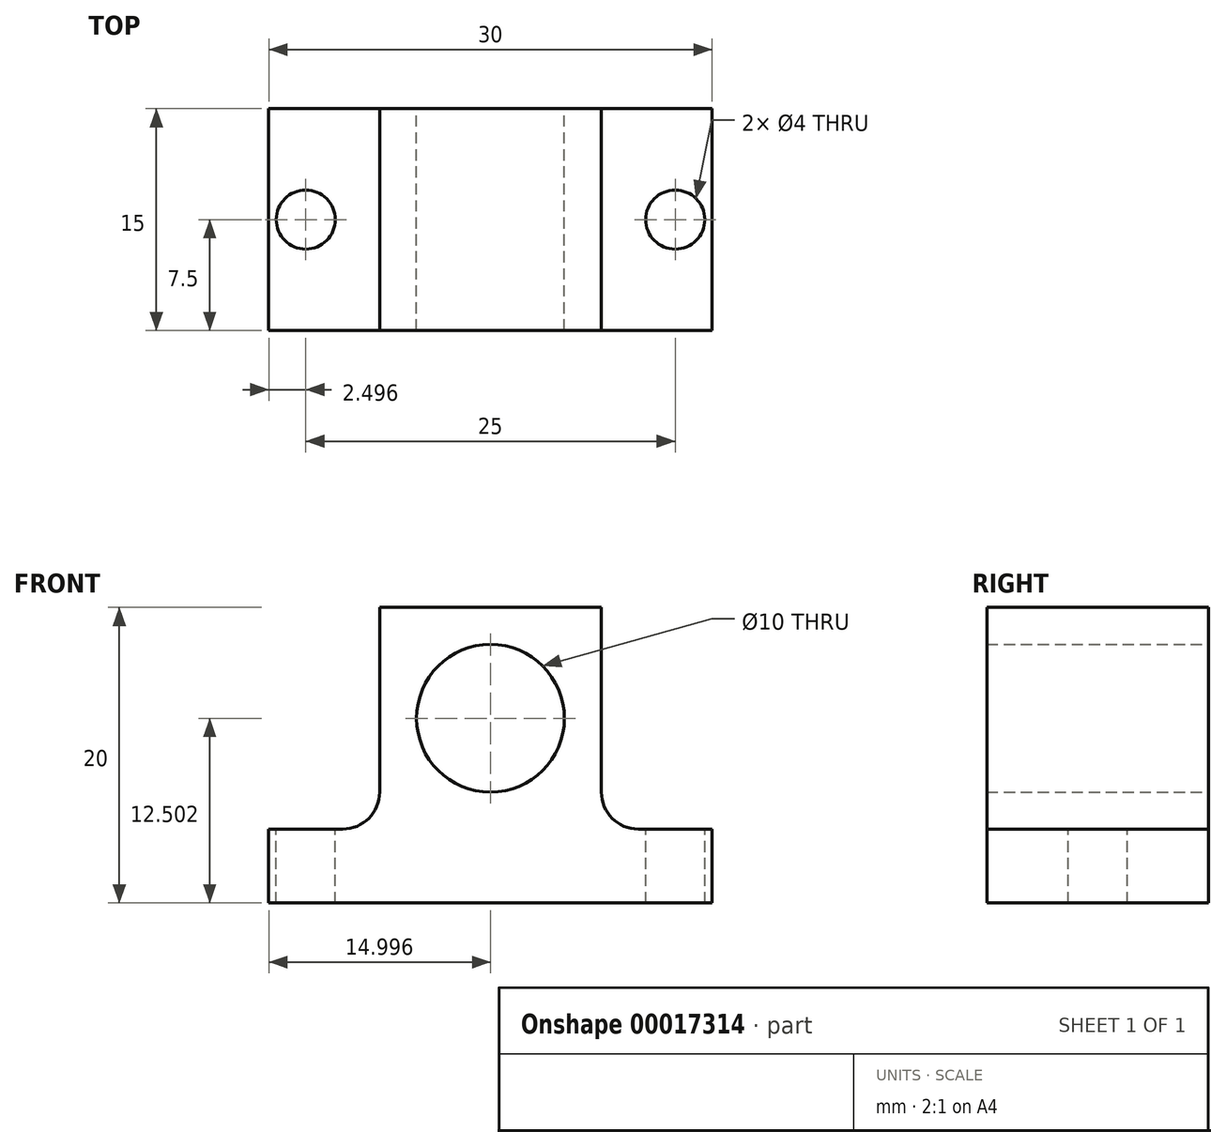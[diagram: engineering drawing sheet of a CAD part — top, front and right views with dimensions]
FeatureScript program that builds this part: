
annotation { "Feature Type Name" : "Feature", "Feature Type Description" : "" }
export const myFeature = defineFeature(function(context is Context, id is Id, definition is map)
    precondition{}
    {
        {
            var Q0;
            Q0=qCreatedBy(makeId("Front.planeOp"),FACE);
            var sketch = newSketch(context, id + "F0", { "sketchPlane" : qUnion([Q0])});
            skLineSegment(sketch, "E0", {"start": v(-38.48, -4.95) * mm, "end": v(-33.48, -4.95) * mm});
            skLineSegment(sketch, "E1", {"start": v(-30.98, -2.45) * mm, "end": v(-30.98, 10.05) * mm});
            skPoint(sketch, "E2.visualSharp", {"position": v(-30.98, -4.95) * mm});
            skArc(sketch, "E2.filletArc", {"start": v(-33.48, -4.95) * mm, "mid": v(-31.72, -4.22) * mm, "end": v(-30.98, -2.45) * mm});
            skLineSegment(sketch, "E3", {"start": v(-30.98, 10.05) * mm, "end": v(-15.98, 10.05) * mm});
            skLineSegment(sketch, "E4", {"start": v(-15.98, 10.05) * mm, "end": v(-15.98, -2.45) * mm});
            skLineSegment(sketch, "E5", {"start": v(-13.48, -4.95) * mm, "end": v(-8.48, -4.95) * mm});
            skPoint(sketch, "E6.visualSharp", {"position": v(-15.98, -4.95) * mm});
            skArc(sketch, "E6.filletArc", {"start": v(-15.98, -2.45) * mm, "mid": v(-15.25, -4.22) * mm, "end": v(-13.48, -4.95) * mm});
            skLineSegment(sketch, "E7", {"start": v(-8.48, -4.95) * mm, "end": v(-8.48, -9.95) * mm});
            skLineSegment(sketch, "E8", {"start": v(-8.48, -9.95) * mm, "end": v(-38.48, -9.95) * mm});
            skLineSegment(sketch, "E9", {"start": v(-38.48, -9.95) * mm, "end": v(-38.48, -4.95) * mm});
            skSolve(sketch);
        }
        {
            var Q0;
            Q0=makeQuery(id+"F0.imprint","IMPRINT",FACE,{"disambiguationData":[TD([[makeQuery(id+"F0.imprint","IMPRINT",EDGE,{"derivedFrom":sQuery(id+"F0.wireOp",EDGE,"E0")}),-1.0]])]});
            extrude(context, id + "F1", {"entities" : qUnion([Q0]), "depth" : 15 * mm});
        }
        {
            var Q0;
            Q0=qCreatedBy(makeId("Front.planeOp"),FACE);
            var sketch = newSketch(context, id + "F2", { "sketchPlane" : qUnion([Q0])});
            skCircle(sketch, "E10", {"center": v(-23.48, 2.55) * mm, "radius": 5 * mm});
            skSolve(sketch);
        }
        {
            var Q0;
            Q0=makeQuery(id+"F2.imprint","IMPRINT",FACE,{"disambiguationData":[TD([[makeQuery(id+"F2.imprint","IMPRINT",EDGE,{"derivedFrom":sQuery(id+"F2.wireOp",EDGE,"E10")}),1.0]])]});
            extrude(context, id + "F3", {"entities" : qUnion([Q0]), "operationType" : NewBodyOperationType.REMOVE, "depth" : 15 * mm});
        }
        {
            var Q0;
            Q0=makeQuery(id+"F1.opExtrude","SWEPT_FACE",FACE,{"disambiguationData":[OSD([sQuery(id+"F0.wireOp",EDGE,"E5")])]});
            var sketch = newSketch(context, id + "F4", { "sketchPlane" : qUnion([Q0])});
            skCircle(sketch, "E11", {"center": v(-10.98, -7.5) * mm, "radius": 2 * mm});
            skSolve(sketch);
        }
        {
            var Q0;
            Q0=makeQuery(id+"F4.imprint","IMPRINT",FACE,{"disambiguationData":[TD([[makeQuery(id+"F4.imprint","IMPRINT",EDGE,{"derivedFrom":sQuery(id+"F4.wireOp",EDGE,"E11")}),1.0]])]});
            extrude(context, id + "F5", {"entities" : qUnion([Q0]), "operationType" : NewBodyOperationType.REMOVE, "oppositeDirection" : true, "depth" : 5 * mm});
        }
        {
            var Q0;
            Q0=makeQuery(id+"F1.opExtrude","SWEPT_FACE",FACE,{"disambiguationData":[OSD([sQuery(id+"F0.wireOp",EDGE,"E0")])]});
            var sketch = newSketch(context, id + "F6", { "sketchPlane" : qUnion([Q0])});
            skCircle(sketch, "E12", {"center": v(-35.98, -7.5) * mm, "radius": 2 * mm});
            skSolve(sketch);
        }
        {
            var Q0;
            Q0=makeQuery(id+"F6.imprint","IMPRINT",FACE,{"disambiguationData":[TD([[makeQuery(id+"F6.imprint","IMPRINT",EDGE,{"derivedFrom":sQuery(id+"F6.wireOp",EDGE,"E12")}),1.0]])]});
            extrude(context, id + "F7", {"entities" : qUnion([Q0]), "operationType" : NewBodyOperationType.REMOVE, "oppositeDirection" : true, "depth" : 5 * mm});
        }
    });
